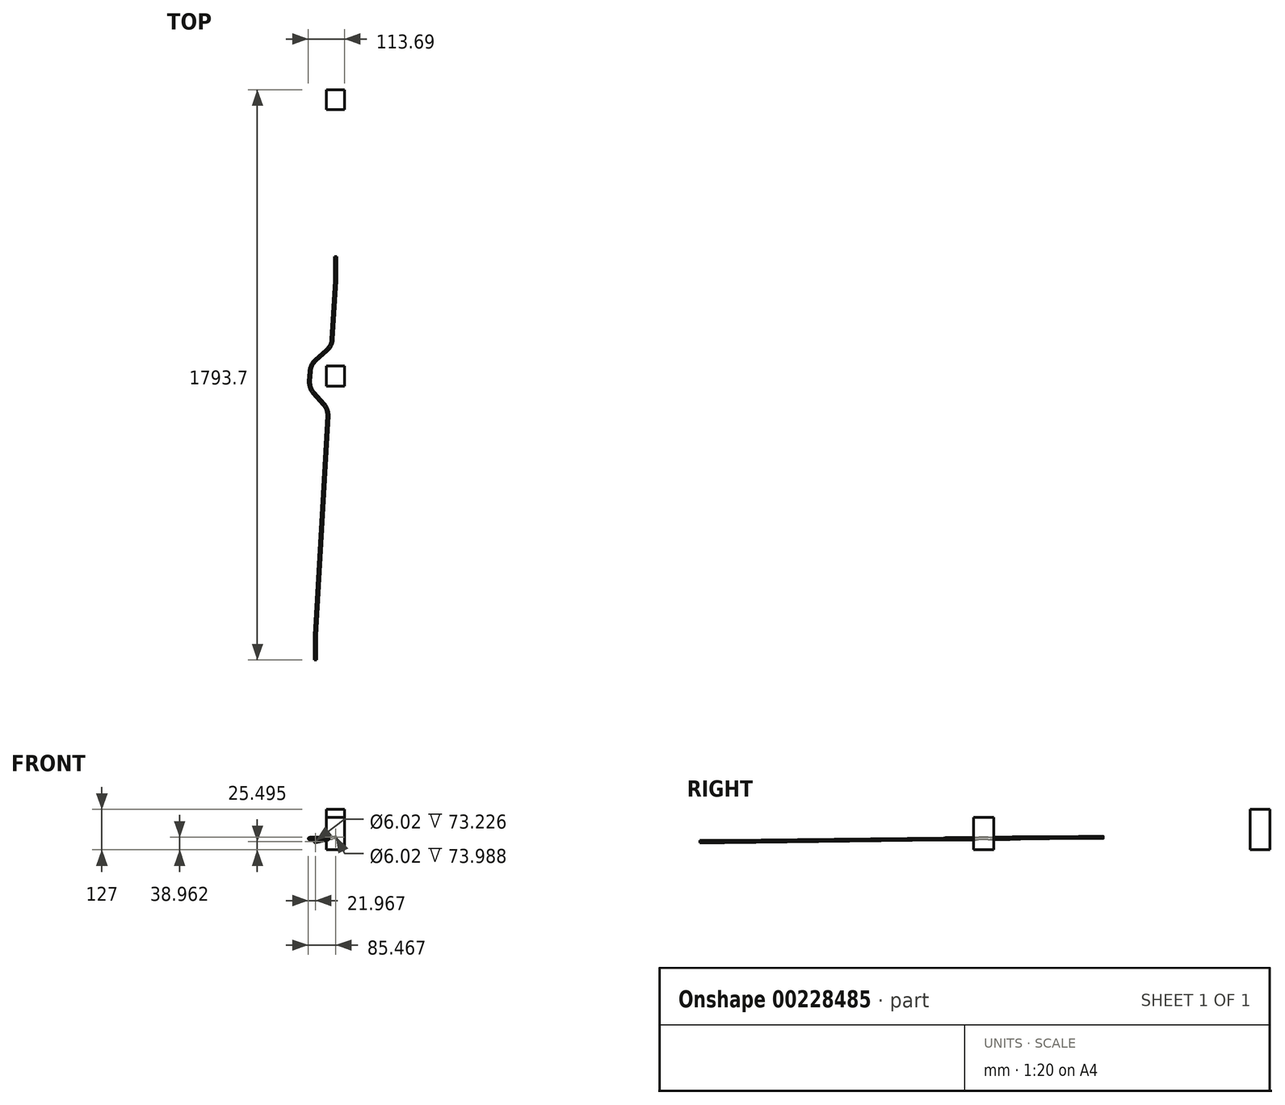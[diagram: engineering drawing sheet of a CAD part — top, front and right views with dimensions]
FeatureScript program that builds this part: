
annotation { "Feature Type Name" : "Feature", "Feature Type Description" : "" }
export const myFeature = defineFeature(function(context is Context, id is Id, definition is map)
    precondition{}
    {
        {
            var Q0;
            Q0=qCreatedBy(makeId("Top.planeOp"),FACE);
            var sketch = newSketch(context, id + "F0", { "sketchPlane" : qUnion([Q0])});
            skLineSegment(sketch, "E0", {"start": v(0, 0) * mm, "end": v(0.27, 0) * mm});
            skLineSegment(sketch, "E1", {"start": v(0.27, 0) * mm, "end": v(0.27, -58.44) * mm});
            skLineSegment(sketch, "E2", {"start": v(0.27, -58.44) * mm, "end": v(25.67, -58.44) * mm});
            skLineSegment(sketch, "E3", {"start": v(0, 0) * mm, "end": v(-63.23, 0) * mm});
            skLineSegment(sketch, "E4", {"start": v(-63.23, 0) * mm, "end": v(-63.23, -1327.88) * mm});
            skLineSegment(sketch, "E5", {"start": v(-63.23, -1327.88) * mm, "end": v(-37.83, -1327.88) * mm});
            skSolve(sketch);
        }
        {
            var Q0;
            Q0=sQuery(id+"F0.wireOp",EDGE,"E5");
            cPlane(context, id + "F1", {"entities" : qUnion([Q0]), "cplaneType" : CPlaneType.LINE_ANGLE, "offset" : 25.4 * mm, "angle" : 0 * degree, "width" : 152.4 * mm, "height" : 152.4 * mm});
        }
        {
            var Q0;
            Q0=sQuery(id+"F0.wireOp",EDGE,"E2");
            cPlane(context, id + "F2", {"entities" : qUnion([Q0]), "cplaneType" : CPlaneType.LINE_ANGLE, "offset" : 25.4 * mm, "angle" : 0 * degree, "width" : 152.4 * mm, "height" : 152.4 * mm});
        }
        {
            var Q0;
            Q0=qCreatedBy(id+"F2.planeOp",FACE);
            var sketch = newSketch(context, id + "F3", { "sketchPlane" : qUnion([Q0])});
            skLineSegment(sketch, "E6", {"start": v(-0.27, 0) * mm, "end": v(-0.27, 811.2) * mm});
            skSolve(sketch);
        }
        {
            var Q0;
            Q0=qCreatedBy(id+"F1.planeOp",FACE);
            var sketch = newSketch(context, id + "F4", { "sketchPlane" : qUnion([Q0])});
            skLineSegment(sketch, "E7", {"start": v(63.23, 0) * mm, "end": v(63.23, 797.74) * mm});
            skSolve(sketch);
        }
        {
            var Q0;
            Q0=sQuery(id+"F3.wireOp",EDGE,"E6");
            cPlane(context, id + "F5", {"entities" : qUnion([Q0]), "cplaneType" : CPlaneType.LINE_ANGLE, "offset" : 25.4 * mm, "angle" : 90 * degree, "width" : 152.4 * mm, "height" : 152.4 * mm});
        }
        {
            var Q0;
            Q0=sQuery(id+"F4.wireOp",EDGE,"E7");
            cPlane(context, id + "F6", {"entities" : qUnion([Q0]), "cplaneType" : CPlaneType.LINE_ANGLE, "offset" : 25.4 * mm, "angle" : 90 * degree, "width" : 152.4 * mm, "height" : 152.4 * mm});
        }
        {
            var Q0;
            Q0=qCreatedBy(id+"F5.planeOp",FACE);
            var sketch = newSketch(context, id + "F7", { "sketchPlane" : qUnion([Q0])});
            skCircle(sketch, "E8", {"center": v(-0.27, 811.2) * mm, "radius": 3.77 * mm});
            skSolve(sketch);
        }
        {
            var Q0;
            Q0=qCreatedBy(id+"F6.planeOp",FACE);
            var sketch = newSketch(context, id + "F8", { "sketchPlane" : qUnion([Q0])});
            skCircle(sketch, "E9", {"center": v(63.23, 797.74) * mm, "radius": 3.77 * mm});
            skSolve(sketch);
        }
        {
            var Q0;
            Q0=sQuery(id+"F3.wireOp",EDGE,"E6");
            cPlane(context, id + "F9", {"entities" : qUnion([Q0]), "cplaneType" : CPlaneType.LINE_ANGLE, "offset" : 25.4 * mm, "angle" : 0 * degree, "width" : 152.4 * mm, "height" : 152.4 * mm});
        }
        {
            var Q0;
            Q0=sQuery(id+"F4.wireOp",EDGE,"E7");
            cPlane(context, id + "F10", {"entities" : qUnion([Q0]), "cplaneType" : CPlaneType.LINE_ANGLE, "offset" : 25.4 * mm, "angle" : 0 * degree, "width" : 152.4 * mm, "height" : 152.4 * mm});
        }
        {
            var Q0;
            Q0=qCreatedBy(id+"F9.planeOp",FACE);
            var sketch = newSketch(context, id + "F11", { "sketchPlane" : qUnion([Q0])});
            skLineSegment(sketch, "E10", {"start": v(-58.44, 811.2) * mm, "end": v(-134.64, 811.2) * mm});
            skSolve(sketch);
        }
        {
            var Q0;
            Q0=qCreatedBy(id+"F10.planeOp",FACE);
            var sketch = newSketch(context, id + "F12", { "sketchPlane" : qUnion([Q0])});
            skLineSegment(sketch, "E11", {"start": v(-1327.88, 797.74) * mm, "end": v(-1251.68, 797.74) * mm});
            skSolve(sketch);
        }
        {
            var Q0;
            Q0=sQuery(id+"F11.wireOp",VERTEX,"E10.end");
            var Q1;
            Q1=sQuery(id+"F12.wireOp",VERTEX,"E11.end");
            var Q2;
            Q2=sQuery(id+"F11.wireOp",VERTEX,"E10.start");
            cPlane(context, id + "F13", {"entities" : qUnion([Q0, Q1, Q2]), "cplaneType" : CPlaneType.THREE_POINT, "offset" : 25.4 * mm, "width" : 152.4 * mm, "height" : 152.4 * mm});
        }
        {
            var Q0;
            Q0=qCreatedBy(id+"F13.planeOp",FACE);
            var sketch = newSketch(context, id + "F14", { "sketchPlane" : qUnion([Q0])});
            skLineSegment(sketch, "E12", {"start": v(168.43, -136.85) * mm, "end": v(103.65, -1251.68) * mm});
            skLineSegment(sketch, "E13", {"start": v(168.56, -132.43) * mm, "end": v(168.56, -58.44) * mm});
            skPoint(sketch, "E14.visualSharp", {"position": v(168.56, -134.64) * mm});
            skArc(sketch, "E14.filletArc", {"start": v(168.43, -136.85) * mm, "mid": v(168.53, -134.64) * mm, "end": v(168.56, -132.43) * mm});
            skSolve(sketch);
        }
        {
            var Q0;
            Q0=sQuery(id+"F14.wireOp",EDGE,"E12");
            var Q1;
            Q1=sQuery(id+"F12.wireOp",EDGE,"E11");
            cPlane(context, id + "F15", {"entities" : qUnion([Q0, Q1]), "cplaneType" : CPlaneType.LINE_ANGLE, "offset" : 25.4 * mm, "angle" : 0 * degree, "width" : 152.4 * mm, "height" : 152.4 * mm});
        }
        {
            var Q0;
            Q0=qCreatedBy(id+"F15.planeOp",FACE);
            var sketch = newSketch(context, id + "F16", { "sketchPlane" : qUnion([Q0])});
            skLineSegment(sketch, "E15", {"start": v(103.65, 1327.88) * mm, "end": v(103.65, 1253.9) * mm});
            skLineSegment(sketch, "E16", {"start": v(103.77, 1249.47) * mm, "end": v(168.43, 136.85) * mm});
            skPoint(sketch, "E17.visualSharp", {"position": v(103.65, 1251.68) * mm});
            skArc(sketch, "E17.filletArc", {"start": v(103.65, 1253.9) * mm, "mid": v(103.68, 1251.68) * mm, "end": v(103.77, 1249.47) * mm});
            skSolve(sketch);
        }
        {
            var Q0;
            Q0=makeQuery(id+"F8.imprint","IMPRINT",FACE,{"disambiguationData":[TD([[makeQuery(id+"F8.imprint","IMPRINT",EDGE,{"derivedFrom":sQuery(id+"F8.wireOp",EDGE,"E9")}),1.0]])]});
            var Q1;
            Q1=sQuery(id+"F16.wireOp",EDGE,"E15");
            var Q2;
            Q2=sQuery(id+"F16.wireOp",EDGE,"E17.filletArc");
            var Q3;
            Q3=sQuery(id+"F16.wireOp",EDGE,"E16");
            var Q4;
            Q4=sQuery(id+"F14.wireOp",EDGE,"E14.filletArc");
            var Q5;
            Q5=sQuery(id+"F14.wireOp",EDGE,"E13");
            sweep(context, id + "F17", {"profiles" : qUnion([Q0]), "path" : qUnion([Q1, Q2, Q3, Q4, Q5])});
        }
        {
            var Q0;
            Q0=makeQuery(id+"F17.opSweep","CAP_FACE",FACE,{"disambiguationData":[OSD([sQuery(id+"F8.wireOp",EDGE,"E9"),sQuery(id+"F16.wireOp",VERTEX,"E15.start")])],"isStart":true});
            shell(context, id + "F18", {"entities" : qUnion([Q0]), "thickness" : 0.76 * mm});
        }
        {
            var Q0;
            Q0=qCreatedBy(makeId("Top.planeOp"),FACE);
            var sketch = newSketch(context, id + "F19", { "sketchPlane" : qUnion([Q0])});
            skLineSegment(sketch, "E18", {"start": v(0, 0) * mm, "end": v(28.44, 0) * mm});
            skLineSegment(sketch, "E19", {"start": v(28.44, 0) * mm, "end": v(28.44, 465.82) * mm});
            skLineSegment(sketch, "E20", {"start": v(28.44, 465.82) * mm, "end": v(3.04, 465.82) * mm});
            skLineSegment(sketch, "E21", {"start": v(0, 0) * mm, "end": v(-27.96, 0) * mm});
            skLineSegment(sketch, "E22", {"start": v(-27.96, 0) * mm, "end": v(-27.96, 403.08) * mm});
            skLineSegment(sketch, "E23", {"start": v(-27.96, 403.08) * mm, "end": v(-53.36, 403.08) * mm});
            skSolve(sketch);
        }
        {
            var Q0;
            Q0=sQuery(id+"F19.wireOp",EDGE,"E20");
            cPlane(context, id + "F20", {"entities" : qUnion([Q0]), "cplaneType" : CPlaneType.LINE_ANGLE, "offset" : 25.4 * mm, "angle" : 0 * degree, "width" : 152.4 * mm, "height" : 152.4 * mm});
        }
        {
            var Q0;
            Q0=sQuery(id+"F19.wireOp",EDGE,"E23");
            cPlane(context, id + "F21", {"entities" : qUnion([Q0]), "cplaneType" : CPlaneType.LINE_ANGLE, "offset" : 25.4 * mm, "angle" : 0 * degree, "width" : 152.4 * mm, "height" : 152.4 * mm});
        }
        {
            var Q0;
            Q0=qCreatedBy(id+"F20.planeOp",FACE);
            var sketch = newSketch(context, id + "F22", { "sketchPlane" : qUnion([Q0])});
            skLineSegment(sketch, "E24", {"start": v(28.44, 0) * mm, "end": v(28.44, 772.24) * mm});
            skSolve(sketch);
        }
        {
            var Q0;
            Q0=qCreatedBy(id+"F21.planeOp",FACE);
            var sketch = newSketch(context, id + "F23", { "sketchPlane" : qUnion([Q0])});
            skLineSegment(sketch, "E25", {"start": v(-27.96, 0) * mm, "end": v(-27.96, 772.24) * mm});
            skLineSegment(sketch, "E26", {"start": v(-27.96, 772.24) * mm, "end": v(-53.36, 772.24) * mm});
            skSolve(sketch);
        }
        {
            var Q0;
            Q0=sQuery(id+"F23.wireOp",EDGE,"E26");
            cPlane(context, id + "F24", {"entities" : qUnion([Q0]), "cplaneType" : CPlaneType.LINE_ANGLE, "offset" : 25.4 * mm, "angle" : 90 * degree, "width" : 152.4 * mm, "height" : 152.4 * mm});
        }
        {
            var Q0;
            Q0=qCreatedBy(id+"F24.planeOp",FACE);
            var sketch = newSketch(context, id + "F25", { "sketchPlane" : qUnion([Q0])});
            skLineSegment(sketch, "E27.bottom", {"start": v(-27.96, 403.08) * mm, "end": v(28.44, 403.08) * mm});
            skLineSegment(sketch, "E27.top", {"start": v(-27.96, 465.82) * mm, "end": v(28.44, 465.82) * mm});
            skLineSegment(sketch, "E27.left", {"start": v(-27.96, 403.08) * mm, "end": v(-27.96, 465.82) * mm});
            skLineSegment(sketch, "E27.right", {"start": v(28.44, 403.08) * mm, "end": v(28.44, 465.82) * mm});
            skSolve(sketch);
        }
        {
            var Q0;
            Q0 = qSketchRegion(id + "F25", true);
            extrude(context, id + "F26", {"entities" : qUnion([Q0]), "depth" : 127 * mm});
        }
        {
            var Q0;
            Q0=qCreatedBy(makeId("Top.planeOp"),FACE);
            var sketch = newSketch(context, id + "F27", { "sketchPlane" : qUnion([Q0])});
            skLineSegment(sketch, "E28", {"start": v(0, 0) * mm, "end": v(28.49, 0) * mm});
            skLineSegment(sketch, "E29", {"start": v(28.49, 0) * mm, "end": v(28.49, -403.6) * mm});
            skLineSegment(sketch, "E30", {"start": v(28.49, -403.6) * mm, "end": v(3.09, -403.6) * mm});
            skLineSegment(sketch, "E31", {"start": v(0, 0) * mm, "end": v(-27.9, 0) * mm});
            skLineSegment(sketch, "E32", {"start": v(-27.9, 0) * mm, "end": v(-27.9, -466.33) * mm});
            skLineSegment(sketch, "E33", {"start": v(-27.9, -466.33) * mm, "end": v(-53.3, -466.33) * mm});
            skSolve(sketch);
        }
        {
            var Q0;
            Q0=sQuery(id+"F27.wireOp",EDGE,"E33");
            cPlane(context, id + "F28", {"entities" : qUnion([Q0]), "cplaneType" : CPlaneType.LINE_ANGLE, "offset" : 25.4 * mm, "angle" : 0 * degree, "width" : 152.4 * mm, "height" : 152.4 * mm});
        }
        {
            var Q0;
            Q0=sQuery(id+"F27.wireOp",EDGE,"E30");
            cPlane(context, id + "F29", {"entities" : qUnion([Q0]), "cplaneType" : CPlaneType.LINE_ANGLE, "offset" : 25.4 * mm, "angle" : 0 * degree, "width" : 152.4 * mm, "height" : 152.4 * mm});
        }
        {
            var Q0;
            Q0=qCreatedBy(id+"F28.planeOp",FACE);
            var sketch = newSketch(context, id + "F30", { "sketchPlane" : qUnion([Q0])});
            skLineSegment(sketch, "E34", {"start": v(-27.9, 0) * mm, "end": v(-27.9, 772.24) * mm});
            skLineSegment(sketch, "E35", {"start": v(-27.9, 772.24) * mm, "end": v(-2.5, 772.24) * mm});
            skSolve(sketch);
        }
        {
            var Q0;
            Q0=qCreatedBy(id+"F29.planeOp",FACE);
            var sketch = newSketch(context, id + "F31", { "sketchPlane" : qUnion([Q0])});
            skLineSegment(sketch, "E36", {"start": v(28.49, 0) * mm, "end": v(28.49, 772.24) * mm});
            skSolve(sketch);
        }
        {
            var Q0;
            Q0=sQuery(id+"F30.wireOp",EDGE,"E35");
            cPlane(context, id + "F32", {"entities" : qUnion([Q0]), "cplaneType" : CPlaneType.LINE_ANGLE, "offset" : 25.4 * mm, "angle" : 90 * degree, "width" : 152.4 * mm, "height" : 152.4 * mm});
        }
        {
            var Q0;
            Q0=qCreatedBy(id+"F32.planeOp",FACE);
            var sketch = newSketch(context, id + "F33", { "sketchPlane" : qUnion([Q0])});
            skLineSegment(sketch, "E37.bottom", {"start": v(-27.9, -466.33) * mm, "end": v(28.49, -466.33) * mm});
            skLineSegment(sketch, "E37.top", {"start": v(-27.9, -403.6) * mm, "end": v(28.49, -403.6) * mm});
            skLineSegment(sketch, "E37.left", {"start": v(-27.9, -466.33) * mm, "end": v(-27.9, -403.6) * mm});
            skLineSegment(sketch, "E37.right", {"start": v(28.49, -466.33) * mm, "end": v(28.49, -403.6) * mm});
            skSolve(sketch);
        }
        {
            var Q0;
            Q0 = qSketchRegion(id + "F33", true);
            extrude(context, id + "F34", {"entities" : qUnion([Q0]), "depth" : 101.6 * mm});
        }
        {
            var Q0;
            Q0=makeQuery(id+"F17.opSweep","SWEPT_BODY",BODY,{"disambiguationData":[OSD([sQuery(id+"F8.wireOp",EDGE,"E9"),sQuery(id+"F14.wireOp",EDGE,"E13")])]});
            deleteBodies(context, id + "F35", {"entities" : qUnion([Q0])});
        }
        {
            var Q0;
            Q0=sQuery(id+"F16.wireOp",EDGE,"E16");
            cPlane(context, id + "F36", {"entities" : qUnion([Q0]), "cplaneType" : CPlaneType.LINE_ANGLE, "offset" : 25.4 * mm, "angle" : 0 * degree, "width" : 152.4 * mm, "height" : 152.4 * mm});
        }
        {
            var Q0;
            Q0=qCreatedBy(id+"F36.planeOp",FACE);
            var sketch = newSketch(context, id + "F37", { "sketchPlane" : qUnion([Q0])});
            skLineSegment(sketch, "E38", {"start": v(-22.75, -529.71) * mm, "end": v(-11.4, -329.93) * mm});
            skLineSegment(sketch, "E39", {"start": v(-27.1, -343.94) * mm, "end": v(-62.7, -375.72) * mm});
            skLineSegment(sketch, "E40", {"start": v(-79.59, -410.73) * mm, "end": v(-81.35, -441.7) * mm});
            skLineSegment(sketch, "E41", {"start": v(-68.53, -478.4) * mm, "end": v(-36.76, -514.01) * mm});
            skLineSegment(sketch, "E42", {"start": v(-82.54, -462.7) * mm, "end": v(-19.14, -466.31) * mm});
            skPoint(sketch, "E43.visualSharp", {"position": v(-78.4, -389.73) * mm});
            skArc(sketch, "E43.filletArc", {"start": v(-62.7, -375.72) * mm, "mid": v(-74.62, -391.55) * mm, "end": v(-79.59, -410.73) * mm});
            skPoint(sketch, "E44.visualSharp", {"position": v(-82.54, -462.7) * mm});
            skArc(sketch, "E44.filletArc", {"start": v(-81.35, -441.7) * mm, "mid": v(-78.59, -461.33) * mm, "end": v(-68.53, -478.4) * mm});
            skLineSegment(sketch, "E45", {"start": v(-23.94, -550.72) * mm, "end": v(-63.1, -1239.77) * mm});
            skLineSegment(sketch, "E46", {"start": v(-10.2, -308.92) * mm, "end": v(0.14, -127.06) * mm});
            skPoint(sketch, "E47.visualSharp", {"position": v(-22.75, -529.71) * mm});
            skArc(sketch, "E47.filletArc", {"start": v(-23.94, -550.72) * mm, "mid": v(-26.7, -531.1) * mm, "end": v(-36.76, -514.01) * mm});
            skPoint(sketch, "E48.visualSharp", {"position": v(-11.4, -329.93) * mm});
            skArc(sketch, "E48.filletArc", {"start": v(-27.1, -343.94) * mm, "mid": v(-15.16, -328.11) * mm, "end": v(-10.2, -308.92) * mm});
            skSolve(sketch);
        }
        {
            var Q0;
            Q0=makeQuery(id+"F7.imprint","IMPRINT",FACE,{"disambiguationData":[TD([[makeQuery(id+"F7.imprint","IMPRINT",EDGE,{"derivedFrom":sQuery(id+"F7.wireOp",EDGE,"E8")}),1.0]])]});
            var Q1;
            Q1=sQuery(id+"F14.wireOp",EDGE,"E13");
            var Q2;
            Q2=sQuery(id+"F14.wireOp",EDGE,"E14.filletArc");
            var Q3;
            Q3=sQuery(id+"F37.wireOp",EDGE,"E46");
            var Q4;
            Q4=sQuery(id+"F37.wireOp",EDGE,"E48.filletArc");
            var Q5;
            Q5=sQuery(id+"F37.wireOp",EDGE,"E39");
            var Q6;
            Q6=sQuery(id+"F37.wireOp",EDGE,"E43.filletArc");
            var Q7;
            Q7=sQuery(id+"F37.wireOp",EDGE,"E40");
            var Q8;
            Q8=sQuery(id+"F37.wireOp",EDGE,"E44.filletArc");
            var Q9;
            Q9=sQuery(id+"F37.wireOp",EDGE,"E41");
            var Q10;
            Q10=sQuery(id+"F37.wireOp",EDGE,"E47.filletArc");
            var Q11;
            Q11=sQuery(id+"F37.wireOp",EDGE,"E45");
            var Q12;
            Q12=sQuery(id+"F16.wireOp",EDGE,"E17.filletArc");
            var Q13;
            Q13=sQuery(id+"F16.wireOp",EDGE,"E15");
            sweep(context, id + "F38", {"profiles" : qUnion([Q0]), "path" : qUnion([Q1, Q2, Q3, Q4, Q5, Q6, Q7, Q8, Q9, Q10, Q11, Q12, Q13])});
        }
        {
            var Q0;
            Q0=makeQuery(id+"F38.opSweep","CAP_FACE",FACE,{"disambiguationData":[OSD([sQuery(id+"F7.wireOp",EDGE,"E8"),sQuery(id+"F14.wireOp",VERTEX,"E13.end")])],"isStart":true});
            shell(context, id + "F39", {"entities" : qUnion([Q0]), "thickness" : 0.76 * mm});
        }
    });
